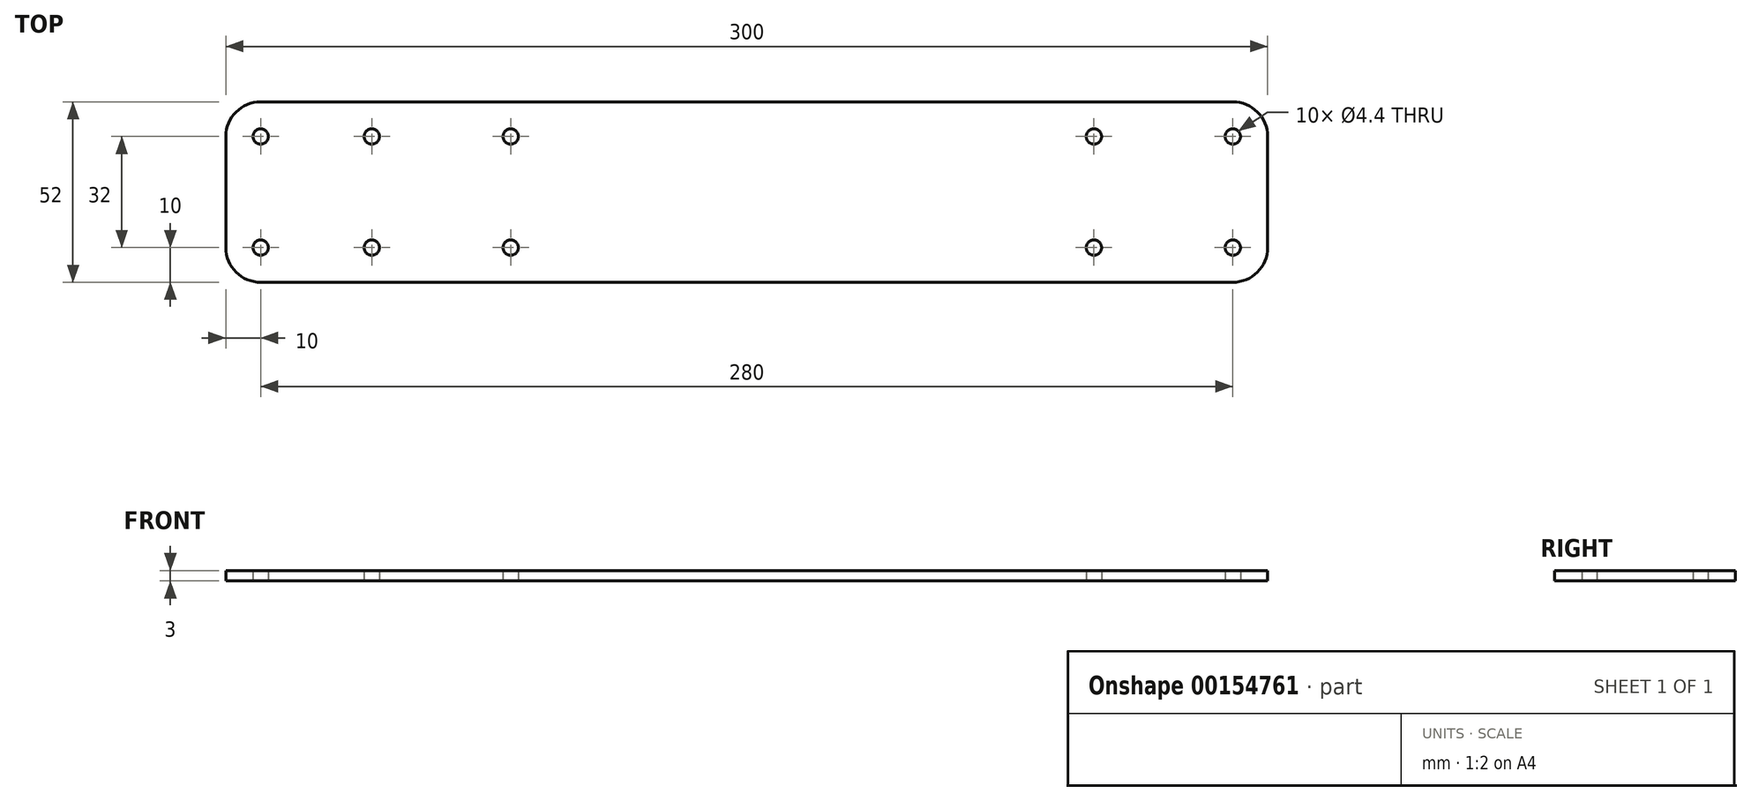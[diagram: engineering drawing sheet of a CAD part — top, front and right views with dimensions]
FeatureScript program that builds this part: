
annotation { "Feature Type Name" : "Feature", "Feature Type Description" : "" }
export const myFeature = defineFeature(function(context is Context, id is Id, definition is map)
    precondition{}
    {
        {
            var Q0;
            Q0=qCreatedBy(makeId("Top.planeOp"),FACE);
            var sketch = newSketch(context, id + "F0", { "sketchPlane" : qUnion([Q0])});
            skLineSegment(sketch, "E0.bottom", {"start": v(140, -26) * mm, "end": v(-140, -26) * mm});
            skLineSegment(sketch, "E0.top", {"start": v(140, 26) * mm, "end": v(-140, 26) * mm});
            skLineSegment(sketch, "E0.left", {"start": v(150, -16) * mm, "end": v(150, 16) * mm});
            skLineSegment(sketch, "E0.right", {"start": v(-150, -16) * mm, "end": v(-150, 16) * mm});
            skPoint(sketch, "E0.middle", {"position": v(0, 0) * mm});
            skPoint(sketch, "E1.visualSharp", {"position": v(-150, 26) * mm});
            skArc(sketch, "E1.filletArc", {"start": v(-140, 26) * mm, "mid": v(-147.07, 23.07) * mm, "end": v(-150, 16) * mm});
            skPoint(sketch, "E2.visualSharp", {"position": v(-150, -26) * mm});
            skArc(sketch, "E2.filletArc", {"start": v(-150, -16) * mm, "mid": v(-147.07, -23.07) * mm, "end": v(-140, -26) * mm});
            skPoint(sketch, "E3.visualSharp", {"position": v(150, -26) * mm});
            skArc(sketch, "E3.filletArc", {"start": v(140, -26) * mm, "mid": v(147.07, -23.07) * mm, "end": v(150, -16) * mm});
            skPoint(sketch, "E4.visualSharp", {"position": v(150, 26) * mm});
            skArc(sketch, "E4.filletArc", {"start": v(150, 16) * mm, "mid": v(147.07, 23.07) * mm, "end": v(140, 26) * mm});
            skSolve(sketch);
        }
        {
            var Q0;
            Q0=makeQuery(id+"F0.imprint","IMPRINT",FACE,{"disambiguationData":[TD([[makeQuery(id+"F0.imprint","IMPRINT",EDGE,{"derivedFrom":sQuery(id+"F0.wireOp",EDGE,"E0.bottom")}),-1.0]])]});
            extrude(context, id + "F1", {"entities" : qUnion([Q0]), "depth" : 3 * mm});
        }
        {
            var Q0;
            Q0=makeQuery(id+"F1.opExtrude","CAP_FACE",FACE,{"disambiguationData":[OSD([sQuery(id+"F0.wireOp",EDGE,"E0.bottom"),sQuery(id+"F0.wireOp",EDGE,"E0.top"),sQuery(id+"F0.wireOp",EDGE,"E0.left"),sQuery(id+"F0.wireOp",EDGE,"E0.right"),sQuery(id+"F0.wireOp",EDGE,"E1.filletArc"),sQuery(id+"F0.wireOp",EDGE,"E2.filletArc"),sQuery(id+"F0.wireOp",EDGE,"E3.filletArc"),sQuery(id+"F0.wireOp",EDGE,"E4.filletArc")])],"isStart":false});
            var sketch = newSketch(context, id + "F2", { "sketchPlane" : qUnion([Q0])});
            skPoint(sketch, "E5", {"position": v(-140, 16) * mm});
            skLineSegment(sketch, "E6", {"start": v(0, 26) * mm, "end": v(0, -26) * mm});
            skPoint(sketch, "E7.0.1.0", {"position": v(-140, -16) * mm});
            skPoint(sketch, "E7.1.0.0", {"position": v(-108, 16) * mm});
            skPoint(sketch, "E7.1.1.0", {"position": v(-108, -16) * mm});
            skLineSegment(sketch, "E7.direction1", {"start": v(-140, 16) * mm, "end": v(-108, 16) * mm, "construction": true});
            skLineSegment(sketch, "E7.direction2", {"start": v(-140, 16) * mm, "end": v(-140, -16) * mm, "construction": true});
            skPoint(sketch, "E8", {"position": v(140, 16) * mm});
            skPoint(sketch, "E9.0.1.0", {"position": v(140, -16) * mm});
            skPoint(sketch, "E9.1.0.0", {"position": v(100, 16) * mm});
            skPoint(sketch, "E9.1.1.0", {"position": v(100, -16) * mm});
            skLineSegment(sketch, "E9.direction1", {"start": v(140, 16) * mm, "end": v(100, 16) * mm, "construction": true});
            skLineSegment(sketch, "E9.direction2", {"start": v(140, 16) * mm, "end": v(140, -16) * mm, "construction": true});
            skPoint(sketch, "E10", {"position": v(-68, 16) * mm});
            skPoint(sketch, "E11.0.1.0", {"position": v(-68, -16) * mm});
            skLineSegment(sketch, "E11.direction2", {"start": v(-68, 16) * mm, "end": v(-68, -16) * mm, "construction": true});
            skSolve(sketch);
        }
        {
            var Q0;
            Q0=sQuery(id+"F2.wireOp",VERTEX,"E5");
            var Q1;
            Q1=sQuery(id+"F2.wireOp",VERTEX,"E7.0.1.0");
            var Q2;
            Q2=sQuery(id+"F2.wireOp",VERTEX,"E7.1.1.0");
            var Q3;
            Q3=sQuery(id+"F2.wireOp",VERTEX,"E7.1.0.0");
            var Q4;
            Q4=sQuery(id+"F2.wireOp",VERTEX,"E10");
            var Q5;
            Q5=sQuery(id+"F2.wireOp",VERTEX,"E11.0.1.0");
            var Q6;
            Q6=sQuery(id+"F2.wireOp",VERTEX,"E8");
            var Q7;
            Q7=sQuery(id+"F2.wireOp",VERTEX,"E9.1.0.0");
            var Q8;
            Q8=sQuery(id+"F2.wireOp",VERTEX,"E9.1.1.0");
            var Q9;
            Q9=sQuery(id+"F2.wireOp",VERTEX,"E9.0.1.0");
            var Q10;
            Q10=makeQuery(id+"F1.opExtrude","SWEPT_BODY",BODY,{"disambiguationData":[OSD([sQuery(id+"F0.wireOp",EDGE,"E0.bottom"),sQuery(id+"F0.wireOp",EDGE,"E0.top"),sQuery(id+"F0.wireOp",EDGE,"E0.left"),sQuery(id+"F0.wireOp",EDGE,"E0.right"),sQuery(id+"F0.wireOp",EDGE,"E1.filletArc"),sQuery(id+"F0.wireOp",EDGE,"E2.filletArc"),sQuery(id+"F0.wireOp",EDGE,"E3.filletArc"),sQuery(id+"F0.wireOp",EDGE,"E4.filletArc")])]});
            hole(context, id + "F3", {"style" : HoleStyle.SIMPLE, "endStyle" : HoleEndStyle.THROUGH, "standardTappedOrClearance" : lookupTablePath({ "standard" : "ISO", "fit" : "Normal", "size" : "M4", "type" : "Clearance" }), "standardBlindInLast" : lookupTablePath({ "fit" : "Standard", "standard" : "ISO", "size" : "M4", "type" : "Clearance" }), "holeDiameter" : 4.4 * mm, "locations" : qUnion([Q0, Q1, Q2, Q3, Q4, Q5, Q6, Q7, Q8, Q9]), "scope" : qUnion([Q10]), "isTappedThrough" : true, "startStyle" : HoleStartStyle.PART});
        }
    });
